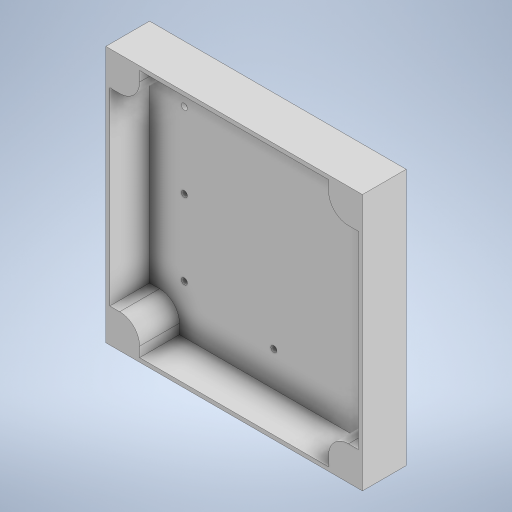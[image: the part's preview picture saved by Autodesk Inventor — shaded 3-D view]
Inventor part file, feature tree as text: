
AUTODESK INVENTOR PART (.ipt)
format: ipt  version: 2023 (Build 270158000, 158)  size: 293,376 bytes
history: native  units: mm
features: sketch x3, extrude x2, hole x1
ambient origin geometry x8: Origin, YZ Plane, XZ Plane, XY Plane, X Axis, Y Axis, Z Axis, Center Point
bodies: Volumenkörper1 (feature_tree)
feature tree (6):
  extrude  "Extrusion1"  Depth=129.0mm
  extrude  "Extrusion2"  Depth=2.0mm
  hole  "Bohrung1"  [1 undecoded]
  sketch  "Skizze1"  dims[d0=129.0mm d1=129.0mm]
  sketch  "Skizze2"  dims[d2=2.0mm d3=0.0mm d4=2.0mm]
  sketch  "Skizze3"  dims[d5=17.0mm d8=10.0mm d9=2.0mm d10=2.0mm d11=2.0mm d12=20.0mm d13=0.0mm d14=76.0mm d15=90.0mm d16=90.0mm d17=3.0mm d18=6.0mm d19=4.0mm d20=2.0mm d21=90.0deg d22=8.0mm d23=20.594885mm]
note: 1 required parameter value undecoded (feature->parameter linkage not recoverable at this tier; creation-order binding heuristic only, values carry confidence <= 0.55)
